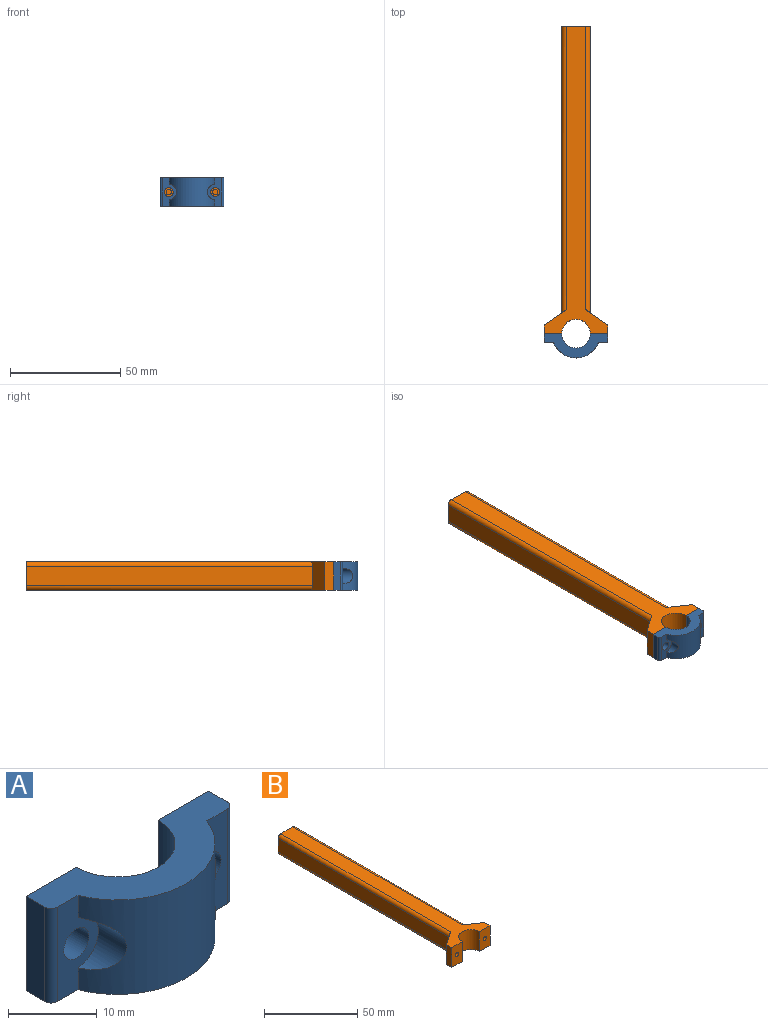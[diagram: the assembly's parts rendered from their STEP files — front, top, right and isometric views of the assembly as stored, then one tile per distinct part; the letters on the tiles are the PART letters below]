
ASSEMBLY  parts=2 mates=1
PART A: 16 faces, bbox 29x11x13 mm
  f0: cylinder r=11mm len=20.49mm, axis (0,0,-1), area 279.6mm2, adj f6,f7,f10,f11,f12,f13
  f1: cylinder r=2mm len=4mm, axis (0,1,0), area 50.3mm2, adj f7,f9
  f2: cylinder r=2mm len=4mm, axis (0,1,0), area 50.3mm2, adj f4,f6
  f3: cylinder r=6.5mm len=13mm, axis (0,0,-1), area 265.5mm2, adj f4,f9,f10,f11
  f4: plane 13x8mm, normal (0,1,0), area 91.4mm2, adj f2,f3,f5,f10,f11
  f5: plane 13x3mm, normal (-1,0,0), area 39mm2, adj f4,f10,f11,f14
  f6: plane 13x6.5mm, normal (0,-1,0), area 47.2mm2, adj f0,f2,f10,f11,f12,f14
  f7: plane 13x6.5mm, normal (0,-1,0), area 47.2mm2, adj f0,f1,f10,f11,f13,f15
  f8: plane 13x3mm, normal (1,0,0), area 39mm2, adj f9,f10,f11,f15
  f9: plane 13x8mm, normal (0,1,0), area 91.4mm2, adj f1,f3,f8,f10,f11
  f10: plane 29x11mm, normal (0,0,1), area 153.3mm2, adj f0,f3,f4,f5,f6,f7,f8,f9
  f11: plane 29x11mm, normal (0,0,-1), area 153.3mm2, adj f0,f3,f4,f5,f6,f7,f8,f9
  f12: cylinder r=3.5mm len=6.98mm, axis (0,1,0), area 33.4mm2, adj f0,f6
  f13: cylinder r=3.5mm len=6.98mm, axis (0,1,0), area 33.4mm2, adj f0,f7
  f14: cylinder r=1mm len=13mm, axis (0,0,-1), area 20.4mm2, adj f5,f6,f10,f11
  f15: cylinder r=1mm len=13mm, axis (0,0,-1), area 20.4mm2, adj f7,f8,f10,f11
PART B: 22 faces, bbox 29x139.5x13 mm
  f0: plane 13x4mm, normal (-1,0,0), area 52mm2, adj f1,f9,f10,f11
  f1: plane 13x8mm, normal (0,-1,0), area 99.1mm2, adj f0,f2,f10,f11,f20
  f2: cylinder r=6.5mm len=13mm, axis (0,0,-1), area 265.5mm2, adj f1,f3,f10,f11
  f3: plane 13x8mm, normal (0,-1,0), area 99.1mm2, adj f2,f4,f10,f11,f18
  f4: plane 13x4mm, normal (1,0,0), area 52mm2, adj f3,f5,f10,f11
  f5: plane 13x10mm, normal (0.57,0.82,0), area 128.2mm2, adj f4,f6,f10,f11,f13,f15
  f6: plane 130x9mm, normal (1,0,0), area 1170mm2, adj f5,f7,f13,f15
  f7: plane 13x13mm, normal (0,1,0), area 79mm2, adj f6,f8,f10,f11,f12,f13,f14,f15
  f8: plane 130x9mm, normal (-1,0,0), area 1170mm2, adj f7,f9,f12,f14
  f9: plane 13x10mm, normal (-0.57,0.82,0), area 128.2mm2, adj f0,f8,f10,f11,f12,f14
  f10: plane 139.49x29mm, normal (0,0,1), area 1337.6mm2, adj f0,f1,f2,f3,f4,f5,f7,f9
  f11: plane 139.49x29mm, normal (0,0,-1), area 1337.6mm2, adj f0,f1,f2,f3,f4,f5,f7,f9
  f12: cylinder r=2mm len=130mm, axis (0,-1,0), area 406.8mm2, adj f7,f8,f9,f11
  f13: cylinder r=2mm len=130mm, axis (0,1,0), area 406.8mm2, adj f5,f6,f7,f11
  f14: cylinder r=2mm len=130mm, axis (0,1,0), area 406.8mm2, adj f7,f8,f9,f10
  f15: cylinder r=2mm len=130mm, axis (0,-1,0), area 406.8mm2, adj f5,f6,f7,f10
  f16: cylinder r=5.25mm len=10.5mm, axis (0,1,0), area 171.5mm2, adj f7,f17
  f17: plane 10.5x10.5mm, normal (0,1,0), area 86.6mm2, adj f16
  f18: cylinder r=1.25mm len=5mm, axis (0,-1,0), area 39.3mm2, adj f3,f19
  f19: plane 2.5x2.5mm, normal (0,-1,0), area 4.9mm2, adj f18
  f20: cylinder r=1.25mm len=5mm, axis (0,-1,0), area 39.3mm2, adj f1,f21
  f21: plane 2.5x2.5mm, normal (0,-1,0), area 4.9mm2, adj f20
PLACE A t=(-3.16,14.8,10.18)mm
PLACE B t=(-3.16,14.8,10.18)mm
MATE slider B.f20 <-> A.f2  axis (0,-1,0) through (-13.66,14.8,16.68)mm
